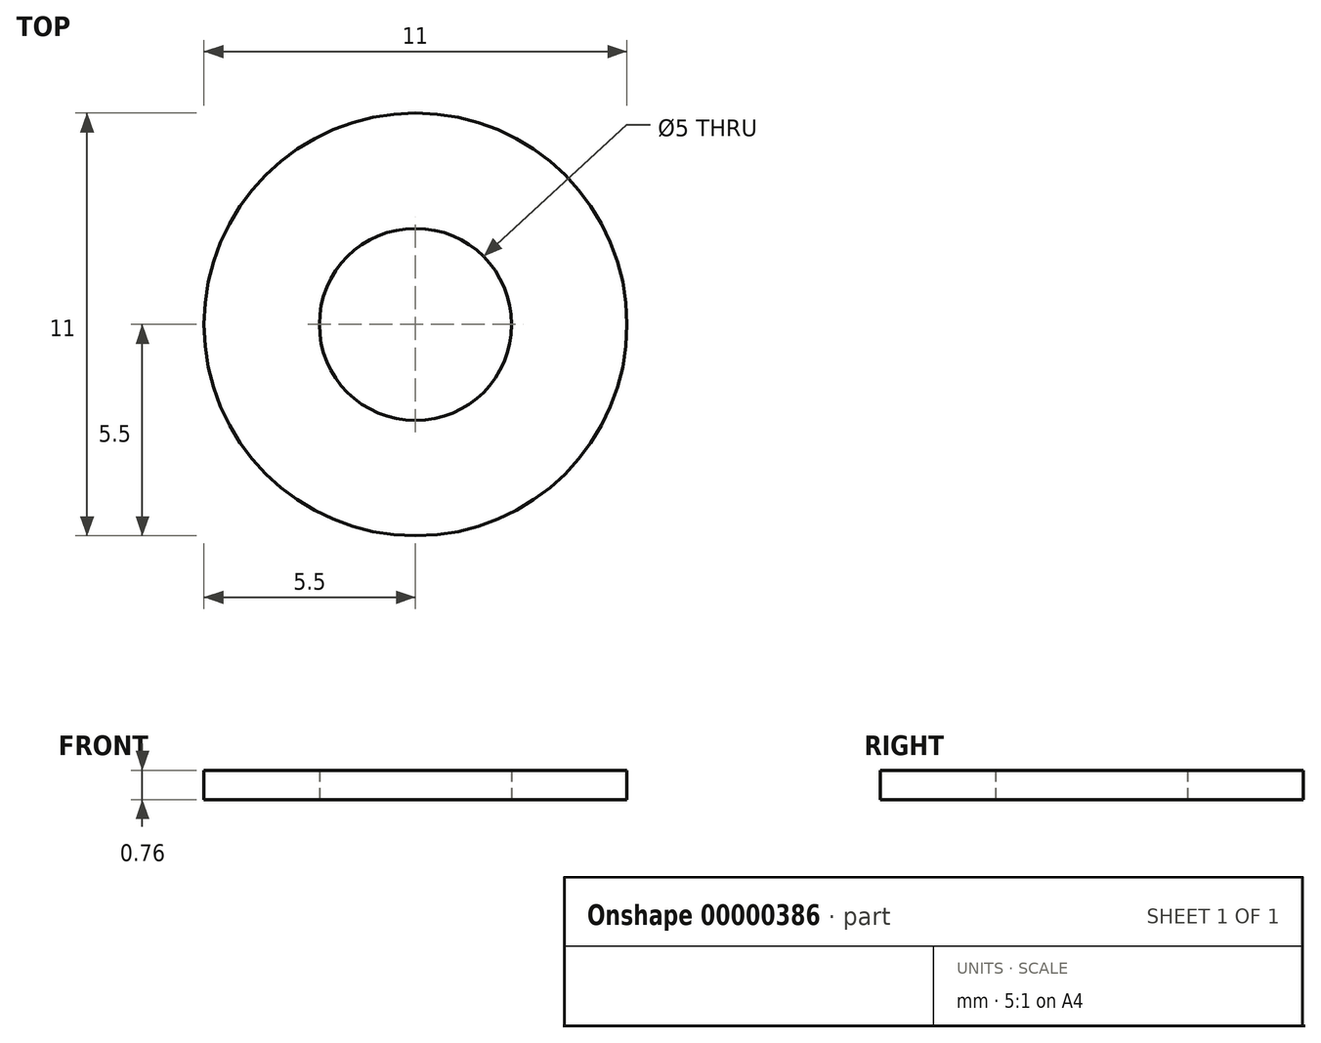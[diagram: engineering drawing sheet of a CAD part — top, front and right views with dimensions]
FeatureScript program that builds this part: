
annotation { "Feature Type Name" : "Feature", "Feature Type Description" : "" }
export const myFeature = defineFeature(function(context is Context, id is Id, definition is map)
    precondition{}
    {
        {
            var Q0;
            Q0=qCreatedBy(makeId("Top.planeOp"),FACE);
            var sketch = newSketch(context, id + "F0", { "sketchPlane" : qUnion([Q0])});
            skCircle(sketch, "E0", {"center": v(0, 0) * mm, "radius": 2.5 * mm});
            skCircle(sketch, "E1", {"center": v(0, 0) * mm, "radius": 5.5 * mm});
            skSolve(sketch);
        }
        {
            var Q0;
            Q0=makeQuery(id+"F0.imprint","IMPRINT",FACE,{"disambiguationData":[TD([[makeQuery(id+"F0.imprint","IMPRINT",EDGE,{"derivedFrom":sQuery(id+"F0.wireOp",EDGE,"E0")}),-1.0]])]});
            extrude(context, id + "F1", {"entities" : qUnion([Q0]), "endBound" : BoundingType.SYMMETRIC, "depth" : 0.76 * mm});
        }
    });
